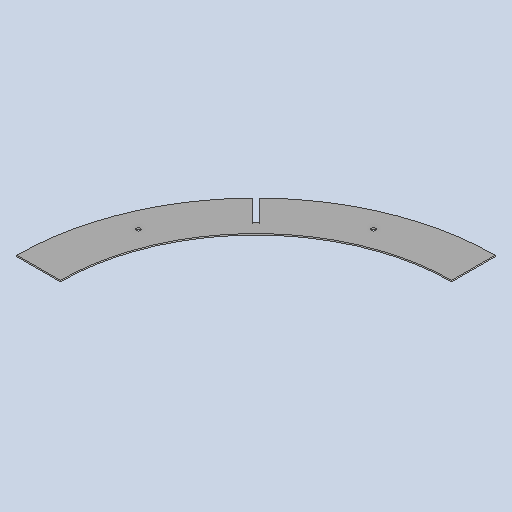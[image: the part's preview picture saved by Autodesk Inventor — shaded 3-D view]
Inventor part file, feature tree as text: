
AUTODESK INVENTOR PART (.ipt)
format: ipt  version: 2025 (Build 290162010, 162A)  size: 311,296 bytes
history: native  units: mm
features: other x4, sketch x3, sheet_metal_op x1, pattern_circular x1, extrude x1
ambient origin geometry x8: Origin, YZ Plane, XZ Plane, XY Plane, X Axis, Y Axis, Z Axis, Center Point
bodies: Solid1 (feature_tree)
feature tree (10):
  other  "BSH 502 segment"
  sheet_metal_op  "Face1"
  pattern_circular  "Circular Pattern1"  Count=110  [1 undecoded]
  extrude  "Extrusion1"  Depth=3.0mm
  sketch  "Sketch1"  dims[d1=900.0mm d2=3.0mm]
  other  "Plate1"
  sketch  "Sketch2"  dims[d4=10.0mm]
  sketch  "Sketch3"  dims[d5=22.5deg d6=3.0mm d7=0.0mm d8=20.0mm d9=45.0deg d11=45.0deg d12=12.0mm d13=70.0mm d14=0.0mm d15=0.0mm]
  other  "Cut1"
  other  "Definition1"
note: 1 required parameter value undecoded (feature->parameter linkage not recoverable at this tier; creation-order binding heuristic only, values carry confidence <= 0.55)
